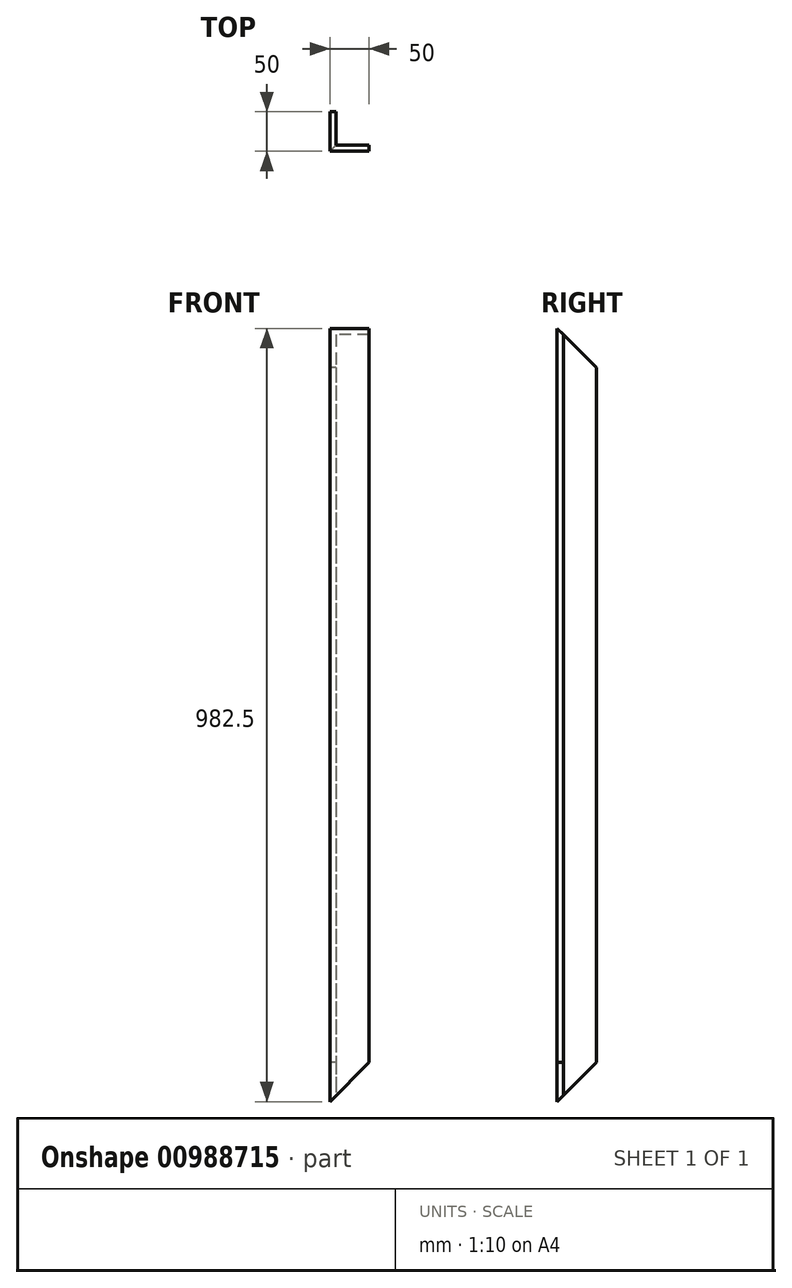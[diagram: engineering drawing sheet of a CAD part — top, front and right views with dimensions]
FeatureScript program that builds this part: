
annotation { "Feature Type Name" : "Feature", "Feature Type Description" : "" }
export const myFeature = defineFeature(function(context is Context, id is Id, definition is map)
    precondition{}
    {
        {
            var Q0;
            Q0=qCreatedBy(makeId("Top.planeOp"),FACE);
            var sketch = newSketch(context, id + "F0", { "sketchPlane" : qUnion([Q0])});
            skLineSegment(sketch, "E0", {"start": v(0, 0) * mm, "end": v(0, 50) * mm});
            skLineSegment(sketch, "E1", {"start": v(0, 50) * mm, "end": v(8, 50) * mm});
            skLineSegment(sketch, "E2", {"start": v(8, 50) * mm, "end": v(8, 8) * mm});
            skLineSegment(sketch, "E3", {"start": v(8, 8) * mm, "end": v(50, 8) * mm});
            skLineSegment(sketch, "E4", {"start": v(50, 8) * mm, "end": v(50, 0) * mm});
            skLineSegment(sketch, "E5", {"start": v(50, 0) * mm, "end": v(0, 0) * mm});
            skSolve(sketch);
        }
        {
            var Q0;
            Q0=qSketchRegion(id+"F0",true);
            extrude(context, id + "F1", {"entities" : qUnion([Q0]), "depth" : 982.5 * mm, "offsetDistance" : 25 * mm});
        }
        {
            var Q0;
            Q0=makeQuery(id+"F1.opExtrude","SWEPT_FACE",FACE,{"disambiguationData":[OSD([sQuery(id+"F0.wireOp",EDGE,"E0")])]});
            var sketch = newSketch(context, id + "F2", { "sketchPlane" : qUnion([Q0])});
            skLineSegment(sketch, "E6", {"start": v(0, 982.5) * mm, "end": v(0, 932.5) * mm});
            skLineSegment(sketch, "E7", {"start": v(0, 932.5) * mm, "end": v(-50, 932.5) * mm});
            skLineSegment(sketch, "E8", {"start": v(-50, 932.5) * mm, "end": v(0, 982.5) * mm});
            skSolve(sketch);
        }
        {
            var Q0;
            {var subQ0=sQuery(id+"F2.wireOp",EDGE,"E8");Q0=makeQuery(id+"F2.imprint","IMPRINT",FACE,{"disambiguationData":[TD([[makeQuery(id+"F2.imprint","IMPRINT",EDGE,{"derivedFrom":subQ0}),1.0]])]});}
            var Q1;
            Q1=makeQuery(id+"F1.opExtrude","SWEPT_FACE",FACE,{"disambiguationData":[OSD([sQuery(id+"F0.wireOp",EDGE,"E2")])]});
            extrude(context, id + "F3", {"entities" : qUnion([Q0]), "operationType" : NewBodyOperationType.REMOVE, "endBound" : BoundingType.THROUGH_ALL, "oppositeDirection" : true, "depth" : 25 * mm, "endBoundEntityFace" : qUnion([Q1]), "offsetDistance" : 25 * mm});
        }
        {
            var Q0;
            Q0=makeQuery(id+"F1.opExtrude","SWEPT_FACE",FACE,{"disambiguationData":[OSD([sQuery(id+"F0.wireOp",EDGE,"E5")])]});
            var sketch = newSketch(context, id + "F4", { "sketchPlane" : qUnion([Q0])});
            skLineSegment(sketch, "E9", {"start": v(0, 0) * mm, "end": v(50, 0) * mm});
            skLineSegment(sketch, "E10", {"start": v(50, 0) * mm, "end": v(50, 50) * mm});
            skLineSegment(sketch, "E11", {"start": v(50, 50) * mm, "end": v(0, 0) * mm});
            skSolve(sketch);
        }
        {
            var Q0;
            Q0=makeQuery(id+"F4.imprint","IMPRINT",FACE,{"disambiguationData":[TD([[makeQuery(id+"F4.imprint","IMPRINT",EDGE,{"derivedFrom":sQuery(id+"F4.wireOp",EDGE,"E9")}),-1.0]])]});
            var Q1;
            Q1=makeQuery(id+"F1.opExtrude","SWEPT_FACE",FACE,{"disambiguationData":[OSD([sQuery(id+"F0.wireOp",EDGE,"E3")])]});
            extrude(context, id + "F5", {"entities" : qUnion([Q0]), "operationType" : NewBodyOperationType.REMOVE, "endBound" : BoundingType.UP_TO_SURFACE, "oppositeDirection" : true, "depth" : 25 * mm, "endBoundEntityFace" : qUnion([Q1]), "offsetDistance" : 25 * mm});
        }
        {
            var Q0;
            Q0=makeQuery(id+"F1.opExtrude","SWEPT_FACE",FACE,{"disambiguationData":[OSD([sQuery(id+"F0.wireOp",EDGE,"E0")])]});
            var sketch = newSketch(context, id + "F6", { "sketchPlane" : qUnion([Q0])});
            skLineSegment(sketch, "E12", {"start": v(0, 0) * mm, "end": v(-50, 0) * mm});
            skLineSegment(sketch, "E13", {"start": v(-50, 0) * mm, "end": v(-50, 50) * mm});
            skLineSegment(sketch, "E14", {"start": v(-50, 50) * mm, "end": v(0, 0) * mm});
            skSolve(sketch);
        }
        {
            var Q0;
            {var subQ3=sQuery(id+"F6.wireOp",EDGE,"E13");Q0=makeQuery(id+"F6.imprint","IMPRINT",FACE,{"disambiguationData":[TD([[makeQuery(id+"F6.imprint","IMPRINT",EDGE,{"derivedFrom":subQ3}),1.0]])]});}
            var Q1;
            Q1=makeQuery(id+"F1.opExtrude","SWEPT_FACE",FACE,{"disambiguationData":[OSD([sQuery(id+"F0.wireOp",EDGE,"E2")])]});
            extrude(context, id + "F7", {"entities" : qUnion([Q0]), "operationType" : NewBodyOperationType.REMOVE, "endBound" : BoundingType.UP_TO_SURFACE, "oppositeDirection" : true, "depth" : 25 * mm, "endBoundEntityFace" : qUnion([Q1]), "offsetDistance" : 25 * mm});
        }
    });
